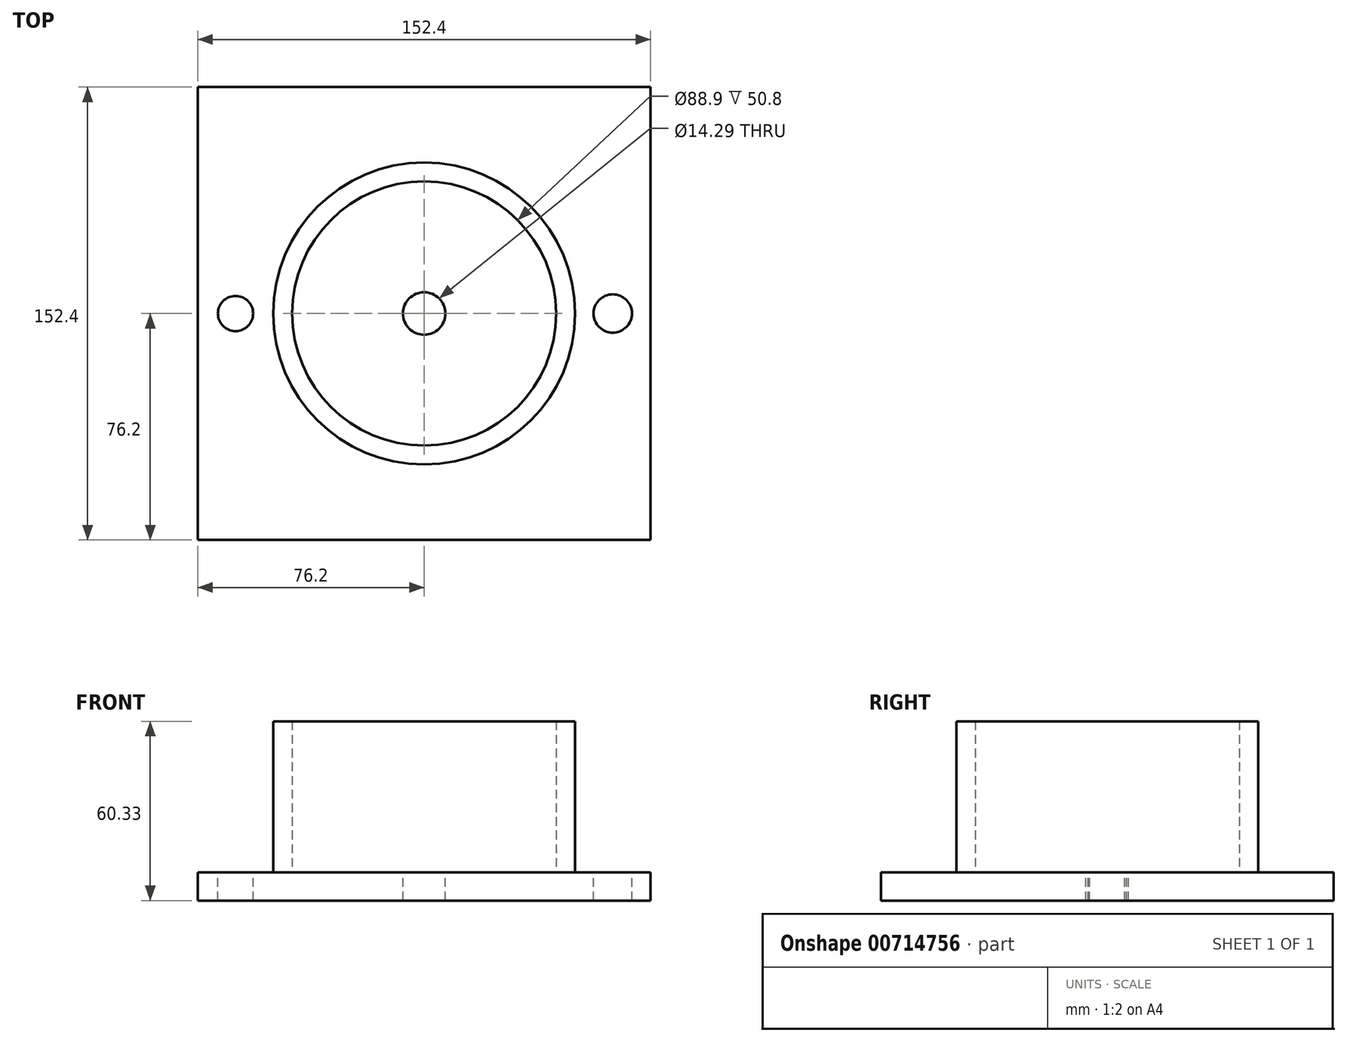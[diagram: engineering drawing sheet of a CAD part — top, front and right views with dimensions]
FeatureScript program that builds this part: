
annotation { "Feature Type Name" : "Feature", "Feature Type Description" : "" }
export const myFeature = defineFeature(function(context is Context, id is Id, definition is map)
    precondition{}
    {
        {
            var Q0;
            Q0=qCreatedBy(makeId("Top.planeOp"),FACE);
            var sketch = newSketch(context, id + "F0", { "sketchPlane" : qUnion([Q0])});
            skLineSegment(sketch, "E0.bottom", {"start": v(76.2, 76.2) * mm, "end": v(-76.2, 76.2) * mm});
            skLineSegment(sketch, "E0.top", {"start": v(76.2, -76.2) * mm, "end": v(-76.2, -76.2) * mm});
            skLineSegment(sketch, "E0.left", {"start": v(76.2, 76.2) * mm, "end": v(76.2, -76.2) * mm});
            skLineSegment(sketch, "E0.right", {"start": v(-76.2, 76.2) * mm, "end": v(-76.2, -76.2) * mm});
            skPoint(sketch, "E0.middle", {"position": v(0, 0) * mm});
            skSolve(sketch);
        }
        {
            var Q0;
            Q0 = qSketchRegion(id + "F0", true);
            extrude(context, id + "F1", {"entities" : qUnion([Q0]), "depth" : 9.52 * mm, "offsetDistance" : 25.4 * mm});
        }
        {
            var Q0;
            Q0=makeQuery(id+"F1.opExtrude","CAP_FACE",FACE,{"disambiguationData":[OSD([sQuery(id+"F0.wireOp",EDGE,"E0.bottom"),sQuery(id+"F0.wireOp",EDGE,"E0.top"),sQuery(id+"F0.wireOp",EDGE,"E0.left"),sQuery(id+"F0.wireOp",EDGE,"E0.right")])],"isStart":false});
            var sketch = newSketch(context, id + "F2", { "sketchPlane" : qUnion([Q0])});
            skCircle(sketch, "E1", {"center": v(0, 0) * mm, "radius": 50.8 * mm});
            skCircle(sketch, "E2", {"center": v(0, 0) * mm, "radius": 44.45 * mm});
            skSolve(sketch);
        }
        {
            var Q0;
            Q0 = qSketchRegion(id + "F2", true);
            extrude(context, id + "F3", {"entities" : qUnion([Q0]), "operationType" : NewBodyOperationType.ADD, "depth" : 50.8 * mm, "offsetDistance" : 25.4 * mm});
        }
        {
            var Q0;
            Q0=makeQuery(id+"F3.boolean.opBoolean","SPLIT",FACE,{"disambiguationData":[TD([makeQuery(id+"F3.opExtrude","SWEPT_FACE",FACE,{"disambiguationData":[OSD([sQuery(id+"F2.wireOp",EDGE,"E2")])]})])],"derivedFrom":makeQuery(id+"F1.opExtrude","CAP_FACE",FACE,{"disambiguationData":[OSD([sQuery(id+"F0.wireOp",EDGE,"E0.bottom"),sQuery(id+"F0.wireOp",EDGE,"E0.top"),sQuery(id+"F0.wireOp",EDGE,"E0.left"),sQuery(id+"F0.wireOp",EDGE,"E0.right")])],"isStart":false})});
            var sketch = newSketch(context, id + "F4", { "sketchPlane" : qUnion([Q0])});
            skCircle(sketch, "E3", {"center": v(0, 0) * mm, "radius": 7.14 * mm});
            skSolve(sketch);
        }
        {
            var Q0;
            Q0 = qSketchRegion(id + "F4", true);
            extrude(context, id + "F5", {"entities" : qUnion([Q0]), "operationType" : NewBodyOperationType.REMOVE, "oppositeDirection" : true, "depth" : 25.4 * mm, "offsetDistance" : 25.4 * mm});
        }
        {
            var Q0;
            {var subQ0=sQuery(id+"F0.wireOp",EDGE,"E0.left");var subQ1=sQuery(id+"F0.wireOp",EDGE,"E0.top");var subQ2=sQuery(id+"F0.wireOp",EDGE,"E0.right");var subQ3=sQuery(id+"F0.wireOp",EDGE,"E0.bottom");Q0=makeQuery(id+"F3.boolean.opBoolean","SPLIT",FACE,{"disambiguationData":[TD([makeQuery(id+"F1.opExtrude","SWEPT_FACE",FACE,{"disambiguationData":[OSD([subQ3])]})])],"derivedFrom":makeQuery(id+"F1.opExtrude","CAP_FACE",FACE,{"disambiguationData":[OSD([subQ3,subQ1,subQ0,subQ2])],"isStart":false})});}
            var sketch = newSketch(context, id + "F6", { "sketchPlane" : qUnion([Q0])});
            skCircle(sketch, "E4", {"center": v(63.5, 0) * mm, "radius": 6.46 * mm});
            skCircle(sketch, "E5", {"center": v(-63.5, 0) * mm, "radius": 5.92 * mm});
            skSolve(sketch);
        }
        {
            var Q0;
            Q0 = qSketchRegion(id + "F6", true);
            extrude(context, id + "F7", {"entities" : qUnion([Q0]), "operationType" : NewBodyOperationType.REMOVE, "oppositeDirection" : true, "depth" : 25.4 * mm, "offsetDistance" : 25.4 * mm});
        }
    });
